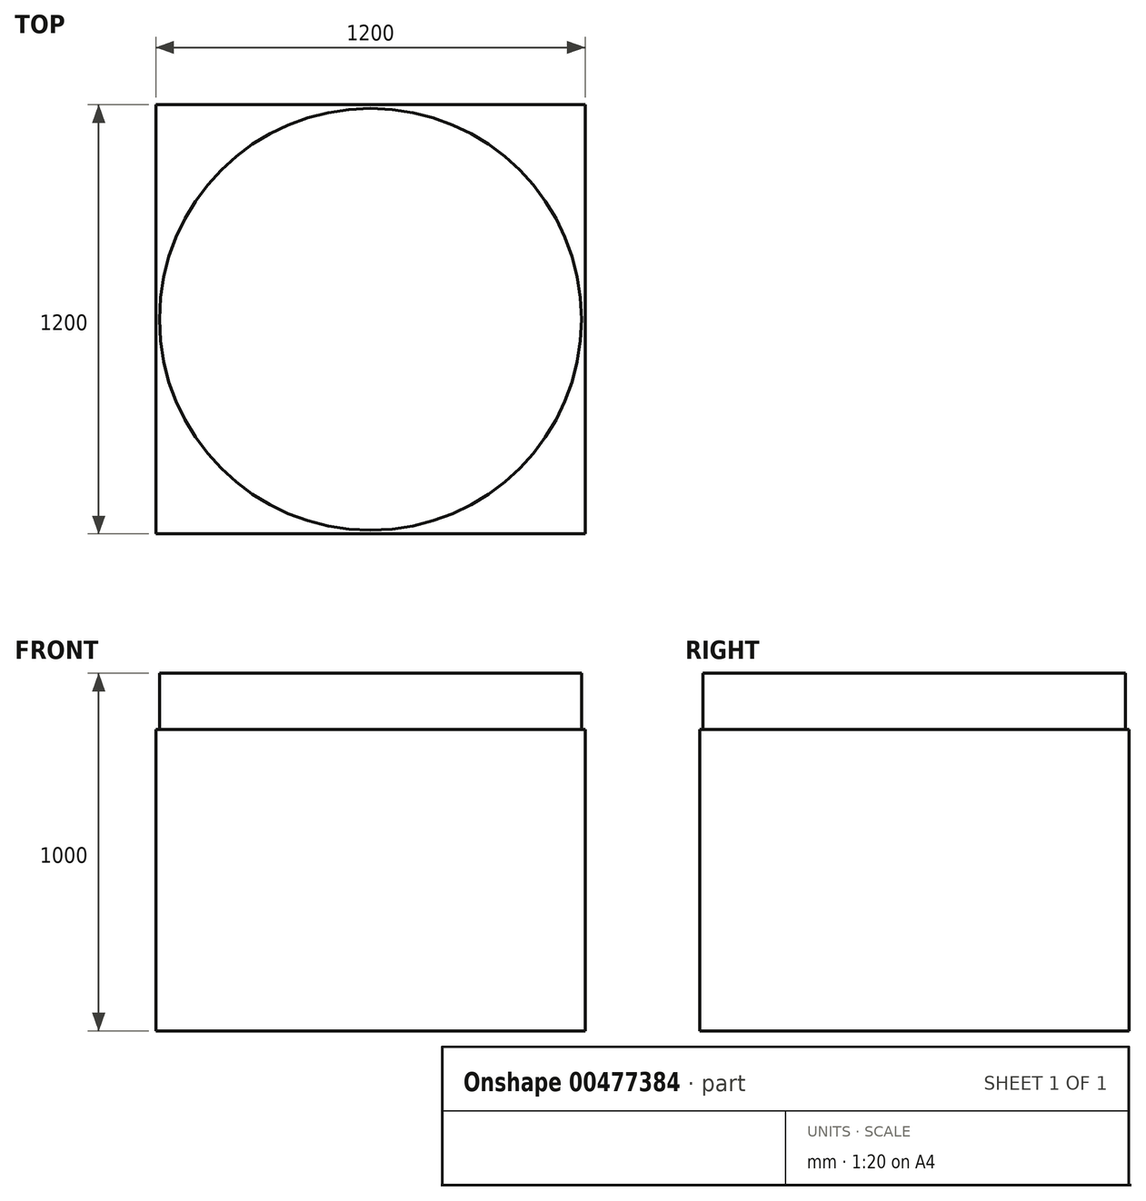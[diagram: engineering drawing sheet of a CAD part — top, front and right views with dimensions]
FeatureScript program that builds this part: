
annotation { "Feature Type Name" : "Feature", "Feature Type Description" : "" }
export const myFeature = defineFeature(function(context is Context, id is Id, definition is map)
    precondition{}
    {
        {
            var Q0;
            Q0=qCreatedBy(makeId("Front.planeOp"),FACE);
            var sketch = newSketch(context, id + "F0", { "sketchPlane" : qUnion([Q0])});
            skLineSegment(sketch, "E0", {"start": v(-600, 0) * mm, "end": v(-600, 842.6) * mm});
            skLineSegment(sketch, "E1", {"start": v(-600, 842.6) * mm, "end": v(-590, 842.6) * mm});
            skLineSegment(sketch, "E2", {"start": v(-590, 842.6) * mm, "end": v(-590, 1000) * mm});
            skLineSegment(sketch, "E3", {"start": v(-590, 1000) * mm, "end": v(0, 1000) * mm});
            skLineSegment(sketch, "E4", {"start": v(0, 1000) * mm, "end": v(0, 0) * mm});
            skLineSegment(sketch, "E5", {"start": v(0, 0) * mm, "end": v(-600, 0) * mm});
            skLineSegment(sketch, "E6", {"start": v(0, 1180.6) * mm, "end": v(0, -205.9) * mm, "construction": true});
            skLineSegment(sketch, "E7", {"start": v(-590, 842.6) * mm, "end": v(0, 842.6) * mm});
            skSolve(sketch);
        }
        {
            var Q0;
            Q0 = qSketchRegion(id + "F0", true);
            var Q1;
            Q1=sQuery(id+"F0.wireOp",EDGE,"E6");
            revolve(context, id + "F1", {"entities" : qUnion([Q0]), "axis" : qUnion([Q1]), "revolveType" : RevolveType.FULL});
        }
        {
            var Q0;
            Q0=makeQuery(id+"F1.opRevolve","SWEPT_FACE",FACE,{"disambiguationData":[OSD([sQuery(id+"F0.wireOp",EDGE,"E5")])]});
            var sketch = newSketch(context, id + "F2", { "sketchPlane" : qUnion([Q0])});
            skLineSegment(sketch, "E8.bottom", {"start": v(600, -600) * mm, "end": v(-600, -600) * mm});
            skLineSegment(sketch, "E8.top", {"start": v(600, 600) * mm, "end": v(-600, 600) * mm});
            skLineSegment(sketch, "E8.left", {"start": v(600, -600) * mm, "end": v(600, 600) * mm});
            skLineSegment(sketch, "E8.right", {"start": v(-600, -600) * mm, "end": v(-600, 600) * mm});
            skPoint(sketch, "E8.middle", {"position": v(0, 0) * mm});
            skSolve(sketch);
        }
        {
            var Q0;
            Q0 = qSketchRegion(id + "F2", true);
            var Q1;
            Q1=makeQuery(id+"F1.opRevolve","SWEPT_FACE",FACE,{"disambiguationData":[OSD([sQuery(id+"F0.wireOp",EDGE,"E1")])]});
            extrude(context, id + "F3", {"entities" : qUnion([Q0]), "operationType" : NewBodyOperationType.ADD, "endBound" : BoundingType.UP_TO_SURFACE, "oppositeDirection" : true, "endBoundEntityFace" : qUnion([Q1]), "depth" : 650 * mm});
        }
    });
